# Revit family: Скамейка «Аэропорт Домодедово» с откидным сиденьем
name_source: partatom
category: Мебель
revit_build: Autodesk Revit 2017 (Build: 20160225_1515(x64)
units: mm (PartAtom-declared; Revit-internal decimal feet)

## family parameters
Всегда вертикально = Да
Заголовок OmniClass = General Furniture and Specialties
На основе рабочей плоскости = Нет
Номер OmniClass = 23.40.20.00
Общий = Нет
При загрузке вырезать с полостями = Нет
Точка расчета площади = Нет

## types (1)
- Скамейка «Аэропорт Домодедово» с откидным сиденьем
    ADSK_Код изделия = 10761
    ADSK_Материал доски = <По категории>
    ADSK_Материал опоры = <По категории>
    ADSK_Материал фурнитуры = <По категории>
    ADSK_Наименование = Скамейка «Аэропорт Домодедово» с откидным сиденьем
    ADSK_Размер_Высота = 967 мм
    ADSK_Размер_Высота сидения = 496 мм
    ADSK_Размер_Длина = 1592 мм
    ADSK_Размер_Ширина = 741 мм
    URL = https://hobbyka.ru
    Длина доски = 1502 мм
    Изготовитель = ООО "Хоббика"
    Стоимость = 197000 $
